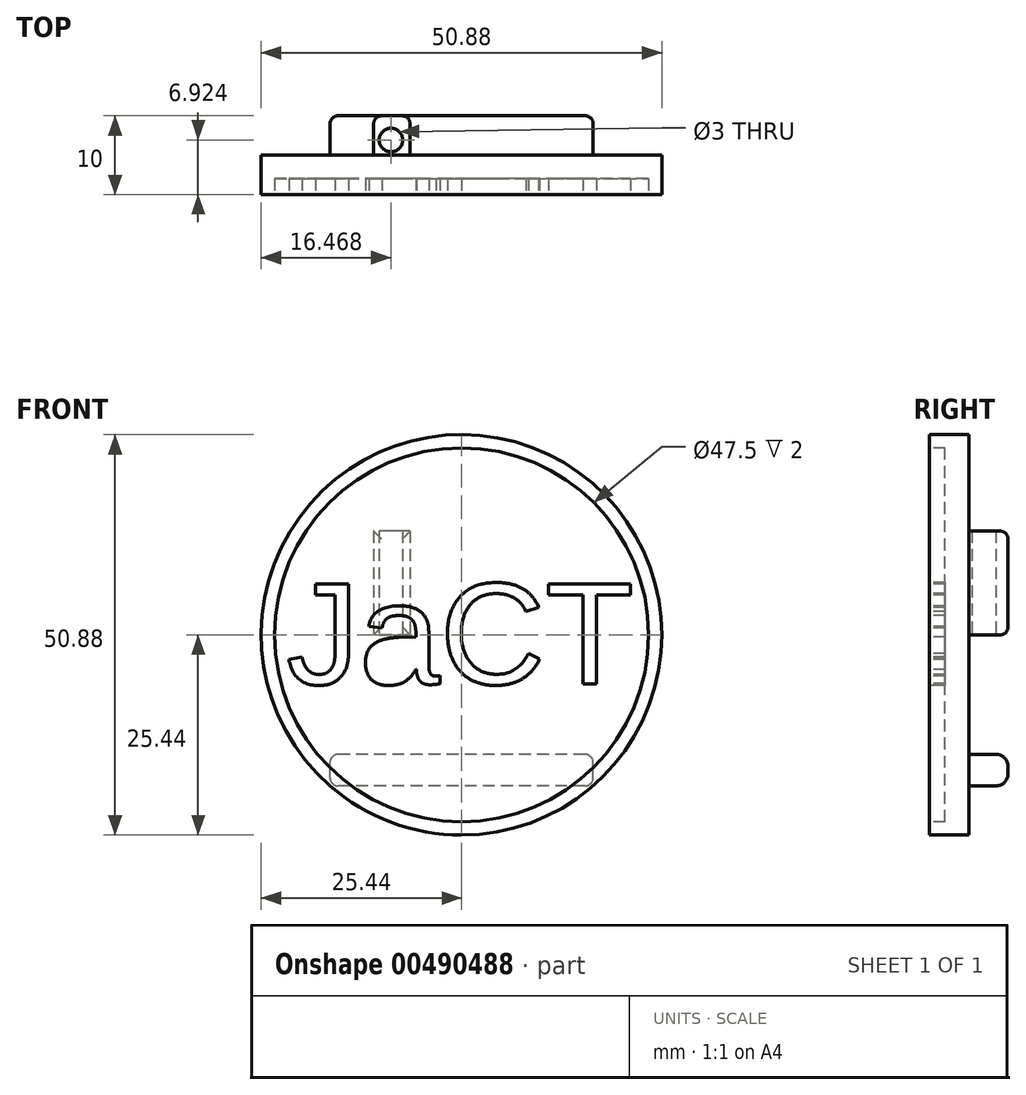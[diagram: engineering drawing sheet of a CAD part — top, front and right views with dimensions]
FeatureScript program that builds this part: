
annotation { "Feature Type Name" : "Feature", "Feature Type Description" : "" }
export const myFeature = defineFeature(function(context is Context, id is Id, definition is map)
    precondition{}
    {
        {
            var Q0;
            Q0=qCreatedBy(makeId("Front.planeOp"),FACE);
            var sketch = newSketch(context, id + "F0", { "sketchPlane" : qUnion([Q0])});
            skCircle(sketch, "E0", {"center": v(0, 0) * mm, "radius": 25.44 * mm});
            skSolve(sketch);
        }
        {
            var Q0;
            Q0=makeQuery(id+"F0.imprint","IMPRINT",FACE,{"disambiguationData":[TD([[makeQuery(id+"F0.imprint","IMPRINT",EDGE,{"derivedFrom":sQuery(id+"F0.wireOp",EDGE,"E0")}),1.0]])]});
            extrude(context, id + "F1", {"entities" : qUnion([Q0]), "depth" : 5 * mm});
        }
        {
            var Q0;
            Q0=makeQuery(id+"F1.opExtrude","CAP_FACE",FACE,{"disambiguationData":[OSD([sQuery(id+"F0.wireOp",EDGE,"E0")])],"isStart":false});
            var sketch = newSketch(context, id + "F2", { "sketchPlane" : qUnion([Q0])});
            skText(sketch, "E1", { "text": "JaCT", "fontName": "Arimo-Regular.ttf"});
            skCircle(sketch, "E2", {"center": v(0, 0) * mm, "radius": 23.75 * mm});
            const initialGuessF2  = {"E1": [-0.02223, -0.00625, 1, 0, 0.0133]};
            skSetInitialGuess(sketch, initialGuessF2);
            skSolve(sketch);
        }
        {
            var Q0;
            Q0 = qSketchRegion(id + "F2", true);
            extrude(context, id + "F3", {"entities" : qUnion([Q0]), "operationType" : NewBodyOperationType.REMOVE, "oppositeDirection" : true, "depth" : 2 * mm});
        }
        {
            var Q0;
            Q0=makeQuery(id+"F1.opExtrude","CAP_FACE",FACE,{"disambiguationData":[OSD([sQuery(id+"F0.wireOp",EDGE,"E0")])],"isStart":true});
            var sketch = newSketch(context, id + "F4", { "sketchPlane" : qUnion([Q0])});
            skLineSegment(sketch, "E3.bottom", {"start": v(6.54, 13.18) * mm, "end": v(11.16, 13.18) * mm});
            skLineSegment(sketch, "E3.top", {"start": v(6.54, 0) * mm, "end": v(11.16, 0) * mm});
            skLineSegment(sketch, "E3.left", {"start": v(6.54, 13.18) * mm, "end": v(6.54, 0) * mm});
            skLineSegment(sketch, "E3.right", {"start": v(11.16, 13.18) * mm, "end": v(11.16, 0) * mm});
            skSolve(sketch);
        }
        {
            var Q0;
            Q0 = qSketchRegion(id + "F4", true);
            extrude(context, id + "F5", {"entities" : qUnion([Q0]), "operationType" : NewBodyOperationType.ADD, "depth" : 5 * mm});
        }
        {
            var Q0;
            Q0=makeQuery(id+"F5.opExtrude","CAP_FACE",FACE,{"disambiguationData":[OSD([sQuery(id+"F4.wireOp",EDGE,"E3.bottom"),sQuery(id+"F4.wireOp",EDGE,"E3.top"),sQuery(id+"F4.wireOp",EDGE,"E3.left"),sQuery(id+"F4.wireOp",EDGE,"E3.right")])],"isStart":false});
            fillet(context, id + "F6", {"entities" : qUnion([Q0]), "radius" : 1 * mm, "tangentPropagation" : true, "allowEdgeOverflow" : false});
        }
        {
            var Q0;
            Q0=qCreatedBy(makeId("Top.planeOp"),FACE);
            var sketch = newSketch(context, id + "F7", { "sketchPlane" : qUnion([Q0])});
            skCircle(sketch, "E4", {"center": v(-8.97, 1.92) * mm, "radius": 1.5 * mm});
            skSolve(sketch);
        }
        {
            var Q0;
            Q0=sQuery(id+"F7.wireOp",VERTEX,"E4.center");
            var Q1;
            Q1=makeQuery(id+"F1.opExtrude","SWEPT_BODY",BODY,{"disambiguationData":[OSD([sQuery(id+"F0.wireOp",EDGE,"E0")])]});
            hole(context, id + "F8", {"style" : HoleStyle.SIMPLE, "endStyle" : HoleEndStyle.THROUGH, "oppositeDirection" : true, "holeDiameter" : 3 * mm, "isTappedThrough" : true, "tappedDepth" : 12 * mm, "tapClearance" : 3, "locations" : qUnion([Q0]), "scope" : qUnion([Q1])});
        }
        {
            var Q0;
            Q0=makeQuery(id+"F1.opExtrude","CAP_FACE",FACE,{"disambiguationData":[OSD([sQuery(id+"F0.wireOp",EDGE,"E0")])],"isStart":true});
            var sketch = newSketch(context, id + "F9", { "sketchPlane" : qUnion([Q0])});
            skLineSegment(sketch, "E5.bottom", {"start": v(-16.71, -19.18) * mm, "end": v(16.71, -19.18) * mm});
            skLineSegment(sketch, "E5.top", {"start": v(-16.71, -15.2) * mm, "end": v(16.71, -15.2) * mm});
            skLineSegment(sketch, "E5.left", {"start": v(-16.71, -19.18) * mm, "end": v(-16.71, -15.2) * mm});
            skLineSegment(sketch, "E5.right", {"start": v(16.71, -19.18) * mm, "end": v(16.71, -15.2) * mm});
            skSolve(sketch);
        }
        {
            var Q0;
            Q0=makeQuery(id+"F9.imprint","IMPRINT",FACE,{"disambiguationData":[TD([[makeQuery(id+"F9.imprint","IMPRINT",EDGE,{"derivedFrom":sQuery(id+"F9.wireOp",EDGE,"E5.bottom")}),1.0]])]});
            extrude(context, id + "F10", {"entities" : qUnion([Q0]), "operationType" : NewBodyOperationType.ADD, "depth" : 5 * mm});
        }
        {
            var Q0;
            Q0=makeQuery(id+"F10.opExtrude","CAP_EDGE",EDGE,{"disambiguationData":[OSD([sQuery(id+"F9.wireOp",EDGE,"E5.top")])],"isStart":false});
            var Q1;
            Q1=makeQuery(id+"F10.opExtrude","CAP_EDGE",EDGE,{"disambiguationData":[OSD([sQuery(id+"F9.wireOp",EDGE,"E5.bottom")])],"isStart":false});
            fillet(context, id + "F11", {"entities" : qUnion([Q0, Q1]), "radius" : 1.5 * mm, "tangentPropagation" : true, "allowEdgeOverflow" : false});
        }
        {
            var Q0;
            Q0=makeQuery(id+"F10.opExtrude","CAP_EDGE",EDGE,{"disambiguationData":[OSD([sQuery(id+"F9.wireOp",EDGE,"E5.left")])],"isStart":false});
            var Q1;
            Q1=makeQuery(id+"F10.opExtrude","CAP_EDGE",EDGE,{"disambiguationData":[OSD([sQuery(id+"F9.wireOp",EDGE,"E5.right")])],"isStart":false});
            fillet(context, id + "F12", {"entities" : qUnion([Q0, Q1]), "radius" : 1 * mm, "tangentPropagation" : true, "allowEdgeOverflow" : false});
        }
    });
